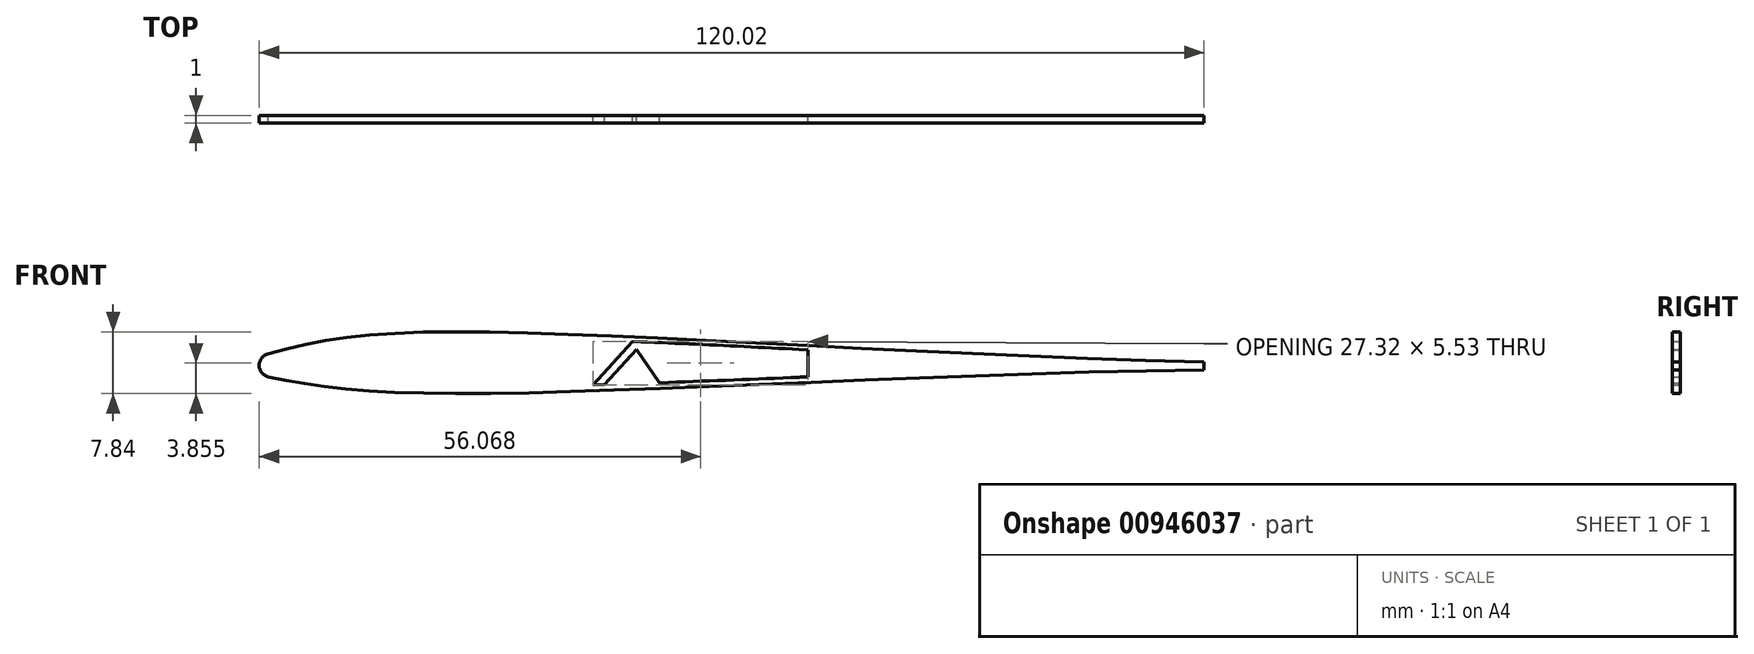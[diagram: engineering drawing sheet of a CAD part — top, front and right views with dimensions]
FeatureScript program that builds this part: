
annotation { "Feature Type Name" : "Feature", "Feature Type Description" : "" }
export const myFeature = defineFeature(function(context is Context, id is Id, definition is map)
    precondition{}
    {
        {
            var Q0;
            Q0=qCreatedBy(makeId("Front.planeOp"),FACE);
            var sketch = newSketch(context, id + "F0", { "sketchPlane" : qUnion([Q0])});
            skPoint(sketch, "E0.middle", {"position": v(0, 0) * mm});
            skPoint(sketch, "E1", {"position": v(-20, 4) * mm});
            skPoint(sketch, "E2", {"position": v(-20, -4) * mm});
            skPoint(sketch, "E3", {"position": v(-63.38, 0) * mm});
            skPoint(sketch, "E4", {"position": v(-38.15, 4.26) * mm});
            skPoint(sketch, "E5", {"position": v(-38.15, -3.52) * mm});
            skArc(sketch, "E6", {"start": v(-58.92, 1.48) * mm, "mid": v(-60, 0.01) * mm, "end": v(-58.88, -1.42) * mm});
            skPoint(sketch, "E6.centerSnap0", {"position": v(-60, 0.03) * mm});
            skPoint(sketch, "E7.orphan", {"position": v(-60, 4.03) * mm});
            skPoint(sketch, "E8.orphan", {"position": v(-60.01, -3.97) * mm});
            skPoint(sketch, "E9.orphan", {"position": v(60.01, 3.97) * mm});
            skPoint(sketch, "E10.orphan", {"position": v(60, -4.03) * mm});
            skCircle(sketch, "E11", {"center": v(-38.37, 0.45) * mm, "radius": 2.2 * mm});
            skLineSegment(sketch, "E12", {"start": v(-35.62, 3.62) * mm, "end": v(-35.62, -2.86) * mm});
            skFitSpline(sketch, "E13", {"points": [v(-58.88, -0.92) * mm, v(-38.13, -2.89) * mm], "startDerivative": vector(19.39, -4.35) * mm, "endDerivative": vector(21.05, -0.35) * mm});
            skFitSpline(sketch, "E14", {"points": [v(-58.92, 1.05) * mm, v(-38.26, 3.62) * mm], "startDerivative": vector(20.55, 5.87) * mm, "endDerivative": vector(18.88, 0.4) * mm});
            skArc(sketch, "E15", {"start": v(-58.92, 1.05) * mm, "mid": v(-59.37, 0.06) * mm, "end": v(-58.88, -0.92) * mm});
            skLineSegment(sketch, "E16", {"start": v(-41.23, -2.81) * mm, "end": v(-41.24, 3.53) * mm});
            skFitSpline(sketch, "E17", {"points": [v(-38.26, 3.62) * mm, v(48.2, 0) * mm], "startDerivative": vector(81.04, 0.3) * mm, "endDerivative": vector(80.8, -3.18) * mm});
            skFitSpline(sketch, "E18", {"points": [v(-38.13, -2.89) * mm, v(48.2, 0) * mm], "startDerivative": vector(80.52, 0.6) * mm, "endDerivative": vector(79.5, 2.02) * mm});
            skLineSegment(sketch, "E19", {"start": v(-17.6, -2.46) * mm, "end": v(-12.57, 3.07) * mm});
            skLineSegment(sketch, "E20", {"start": v(-11.55, 3.07) * mm, "end": v(-8.01, -2.14) * mm});
            skLineSegment(sketch, "E21", {"start": v(-16.13, -2.42) * mm, "end": v(-12.05, 2.06) * mm});
            skLineSegment(sketch, "E22", {"start": v(-12.05, 2.06) * mm, "end": v(-9.17, -2.18) * mm});
            skLineSegment(sketch, "E23", {"start": v(8.59, 2.05) * mm, "end": v(8.59, -1.48) * mm});
            skLineSegment(sketch, "E24", {"start": v(9.72, 1.99) * mm, "end": v(9.72, -1.43) * mm});
            skFitSpline(sketch, "E25.trimOffspring", {"points": [v(-38.26, 3.62) * mm, v(48.2, 0) * mm], "startDerivative": vector(81.04, 0.3) * mm, "endDerivative": vector(80.8, -3.18) * mm});
            skLineSegment(sketch, "E26", {"start": v(60, -0.03) * mm, "end": v(60, 0.47) * mm});
            skLineSegment(sketch, "E27", {"start": v(60, -0.03) * mm, "end": v(60, -0.53) * mm});
            skFitSpline(sketch, "E28", {"points": [v(-58.88, -1.42) * mm, v(-38.15, -3.52) * mm, v(60, -0.53) * mm], "startDerivative": vector(51.85, -10.71) * mm, "endDerivative": vector(168.15, 2.34) * mm});
            skFitSpline(sketch, "E29", {"points": [v(-58.92, 1.48) * mm, v(-38.15, 4.26) * mm, v(60, 0.47) * mm], "startDerivative": vector(55.26, 16.33) * mm, "endDerivative": vector(170.94, -3.98) * mm});
            skSolve(sketch);
        }
        {
            var Q0;
            Q0=makeQuery(id+"F0.imprint","IMPRINT",FACE,{"disambiguationData":[TD([[makeQuery(id+"F0.imprint","IMPRINT",EDGE,{"derivedFrom":sQuery(id+"F0.wireOp",EDGE,"E11")}),-1.0]])]});
            var Q1;
            Q1=makeQuery(id+"F0.imprint","IMPRINT",FACE,{"disambiguationData":[TD([[makeQuery(id+"F0.imprint","IMPRINT",EDGE,{"derivedFrom":sQuery(id+"F0.wireOp",EDGE,"ae7eaf1d-4091-4a16-b937-15f120710b4f")}),-1.0]])]});
            var Q2;
            {var subQ10=sQuery(id+"F0.wireOp",EDGE,"E6");Q2=makeQuery(id+"F0.imprint","IMPRINT",FACE,{"disambiguationData":[TD([[makeQuery(id+"F0.imprint","IMPRINT",EDGE,{"derivedFrom":subQ10}),1.0]])]});}
            var Q3;
            Q3=makeQuery(id+"F0.imprint","IMPRINT",FACE,{"disambiguationData":[TD([[makeQuery(id+"F0.imprint","IMPRINT",EDGE,{"derivedFrom":sQuery(id+"F0.wireOp",EDGE,"2ncaptef-bhzp-t8Xd-6jRW-goQZvCcsXw1w")}),-1.0]])]});
            var Q4;
            {var subQ4=sQuery(id+"F0.wireOp",EDGE,"Ge4f9XJX-EF0X-kTaq-YnlE-pP1QlcMFxq2a");Q4=makeQuery(id+"F0.imprint","IMPRINT",FACE,{"disambiguationData":[TD([[makeQuery(id+"F0.imprint","IMPRINT",EDGE,{"derivedFrom":subQ4}),1.0]])]});}
            var Q5;
            {var subQ0=sQuery(id+"F0.wireOp",EDGE,"E15");Q5=makeQuery(id+"F0.imprint","IMPRINT",FACE,{"disambiguationData":[TD([[makeQuery(id+"F0.imprint","IMPRINT",EDGE,{"derivedFrom":subQ0}),1.0]])]});}
            var Q6;
            {var subQ0=sQuery(id+"F0.wireOp",EDGE,"E12");Q6=makeQuery(id+"F0.imprint","IMPRINT",FACE,{"disambiguationData":[TD([[makeQuery(id+"F0.imprint","IMPRINT",EDGE,{"derivedFrom":subQ0}),1.0]])]});}
            var Q7;
            Q7=makeQuery(id+"F0.imprint","IMPRINT",FACE,{"disambiguationData":[TD([[makeQuery(id+"F0.imprint","IMPRINT",EDGE,{"derivedFrom":sQuery(id+"F0.wireOp",EDGE,"E11")}),1.0]])]});
            var Q8;
            Q8=makeQuery(id+"F0.imprint","IMPRINT",FACE,{"disambiguationData":[TD([[makeQuery(id+"F0.imprint","IMPRINT",EDGE,{"derivedFrom":sQuery(id+"F0.wireOp",EDGE,"E21")}),-1.0]])]});
            var Q9;
            {var subQ2=sQuery(id+"F0.wireOp",EDGE,"E17");Q9=makeQuery(id+"F0.imprint","IMPRINT",FACE,{"disambiguationData":[TD([[makeQuery(id+"F0.imprint","IMPRINT",EDGE,{"derivedFrom":subQ2}),-1.0]])]});}
            var Q10;
            Q10=makeQuery(id+"F0.imprint","IMPRINT",FACE,{"disambiguationData":[TD([[makeQuery(id+"F0.imprint","IMPRINT",EDGE,{"derivedFrom":sQuery(id+"F0.wireOp",EDGE,"E24")}),1.0]])]});
            extrude(context, id + "F1", {"entities" : qUnion([Q0, Q1, Q2, Q3, Q4, Q5, Q6, Q7, Q8, Q9, Q10]), "endBound" : BoundingType.SYMMETRIC, "depth" : 1 * mm, "offsetDistance" : 25 * mm});
        }
    });
